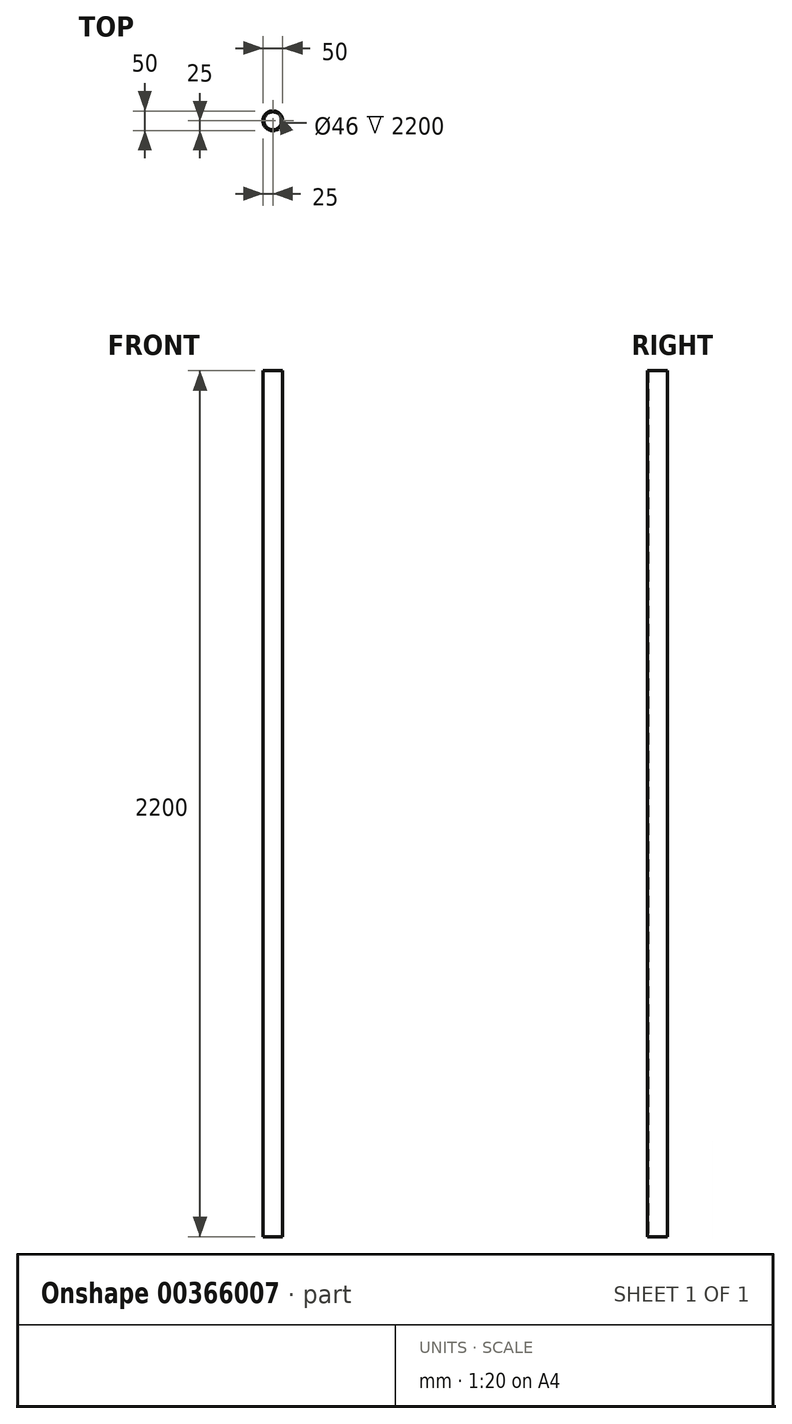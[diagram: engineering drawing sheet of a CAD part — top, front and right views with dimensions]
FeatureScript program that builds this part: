
annotation { "Feature Type Name" : "Feature", "Feature Type Description" : "" }
export const myFeature = defineFeature(function(context is Context, id is Id, definition is map)
    precondition{}
    {
        {
            var Q0;
            Q0=qCreatedBy(makeId("Top.planeOp"),FACE);
            var sketch = newSketch(context, id + "F0", { "sketchPlane" : qUnion([Q0])});
            skCircle(sketch, "E0", {"center": v(0, 0) * mm, "radius": 25 * mm});
            skCircle(sketch, "E1", {"center": v(0, 0) * mm, "radius": 23 * mm});
            skSolve(sketch);
        }
        {
            var Q0;
            Q0=makeQuery(id+"F0.imprint","IMPRINT",FACE,{"disambiguationData":[TD([[makeQuery(id+"F0.imprint","IMPRINT",EDGE,{"derivedFrom":sQuery(id+"F0.wireOp",EDGE,"E0")}),1.0]])]});
            extrude(context, id + "F1", {"entities" : qUnion([Q0]), "depth" : 2200 * mm});
        }
    });
